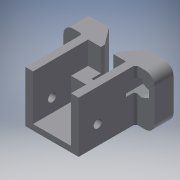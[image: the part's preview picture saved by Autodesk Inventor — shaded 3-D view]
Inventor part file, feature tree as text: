
AUTODESK INVENTOR PART (.ipt)
format: ipt  version: 2018 (Build 220112000, 112)  size: 183,296 bytes
history: native  units: mm
features: sketch x9, other x3
ambient origin geometry x8: Origin, YZ Plane, XZ Plane, XY Plane, X Axis, Y Axis, Z Axis, Center Point
bodies: Solid1 (feature_tree)
feature tree (12):
  other  "holder-GT2-x-carriage-left.ipt"
  other  "Solid1::holder-GT2-x-carriage-left.ipt"
  other  "TaggingFeature1"
  sketch  "Sketch1"  dims[d0=10.0mm]
  sketch  "Sketch2"
  sketch  "Sketch3"
  sketch  "Sketch4"
  sketch  "Sketch8"
  sketch  "Sketch9"
  sketch  "Sketch6"
  sketch  "Sketch11"
  sketch  "Sketch12"
